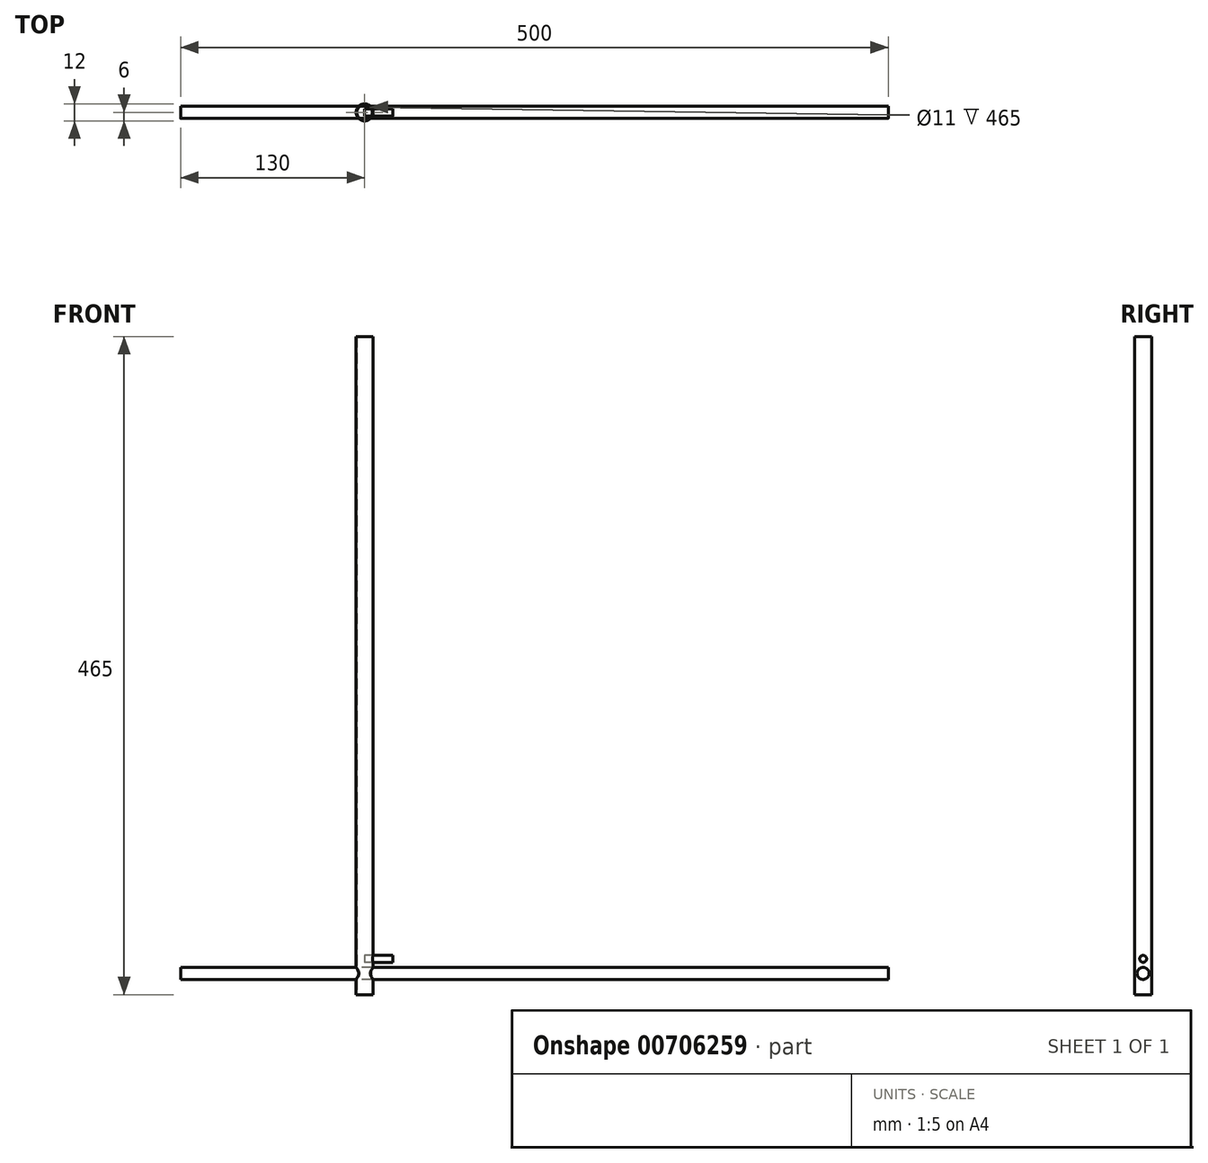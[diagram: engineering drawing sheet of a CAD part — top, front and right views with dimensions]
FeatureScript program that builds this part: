
annotation { "Feature Type Name" : "Feature", "Feature Type Description" : "" }
export const myFeature = defineFeature(function(context is Context, id is Id, definition is map)
    precondition{}
    {
        {
            var Q0;
            Q0=qCreatedBy(makeId("Top.planeOp"),FACE);
            var sketch = newSketch(context, id + "F0", { "sketchPlane" : qUnion([Q0])});
            skCircle(sketch, "E0", {"center": v(0, 0) * mm, "radius": 6 * mm});
            skCircle(sketch, "E1", {"center": v(0, 0) * mm, "radius": 5.5 * mm});
            skSolve(sketch);
        }
        {
            var Q0;
            Q0 = qSketchRegion(id + "F0", true);
            extrude(context, id + "F1", {"entities" : qUnion([Q0]), "depth" : 465 * mm, "offsetDistance" : 25 * mm});
        }
        {
            var Q0;
            Q0=qCreatedBy(makeId("Right.planeOp"),FACE);
            var sketch = newSketch(context, id + "F2", { "sketchPlane" : qUnion([Q0])});
            skCircle(sketch, "E2", {"center": v(0, 25.3) * mm, "radius": 2.44 * mm});
            skSolve(sketch);
        }
        {
            var Q0;
            Q0 = qSketchRegion(id + "F2", true);
            extrude(context, id + "F3", {"entities" : qUnion([Q0]), "operationType" : NewBodyOperationType.ADD, "depth" : 20 * mm, "offsetDistance" : 25 * mm});
        }
        {
            var Q0;
            Q0=qCreatedBy(makeId("Right.planeOp"),FACE);
            var sketch = newSketch(context, id + "F4", { "sketchPlane" : qUnion([Q0])});
            skLineSegment(sketch, "E3", {"start": v(0, 0) * mm, "end": v(0, 15) * mm});
            skCircle(sketch, "E4", {"center": v(0, 15) * mm, "radius": 4.25 * mm});
            skSolve(sketch);
        }
        {
            var Q0;
            Q0=sQuery(id+"F4.wireOp",VERTEX,"E4.center");
            var Q1;
            Q1=makeQuery(id+"F1.opExtrude","SWEPT_BODY",BODY,{"disambiguationData":[OSD([sQuery(id+"F0.wireOp",EDGE,"E0"),sQuery(id+"F0.wireOp",EDGE,"E1")])]});
            hole(context, id + "F5", {"style" : HoleStyle.SIMPLE, "endStyle" : HoleEndStyle.THROUGH, "holeDiameter" : 8 * mm, "majorDiameter" : 5 * mm, "isTappedThrough" : true, "tappedDepth" : 12 * mm, "tapClearance" : 3, "locations" : qUnion([Q0]), "scope" : qUnion([Q1])});
        }
        {
            var Q0;
            Q0=sQuery(id+"F4.wireOp",VERTEX,"E4.center");
            var Q1;
            Q1=makeQuery(id+"F1.opExtrude","SWEPT_BODY",BODY,{"disambiguationData":[OSD([sQuery(id+"F0.wireOp",EDGE,"E0"),sQuery(id+"F0.wireOp",EDGE,"E1")])]});
            hole(context, id + "F6", {"style" : HoleStyle.SIMPLE, "endStyle" : HoleEndStyle.THROUGH, "oppositeDirection" : true, "holeDiameter" : 8 * mm, "majorDiameter" : 5 * mm, "isTappedThrough" : true, "tappedDepth" : 12 * mm, "tapClearance" : 3, "locations" : qUnion([Q0]), "scope" : qUnion([Q1])});
        }
        {
            var Q0;
            Q0 = qSketchRegion(id + "F4", true);
            extrude(context, id + "F7", {"entities" : qUnion([Q0]), "operationType" : NewBodyOperationType.ADD, "endBound" : BoundingType.SYMMETRIC, "depth" : 260 * mm, "offsetDistance" : 25 * mm});
        }
        {
            var Q0;
            Q0=makeQuery(id+"F7.opExtrude","CAP_FACE",FACE,{"disambiguationData":[OSD([sQuery(id+"F4.wireOp",EDGE,"E4")])],"isStart":false});
            extrude(context, id + "F8", {"entities" : qUnion([Q0]), "operationType" : NewBodyOperationType.ADD, "depth" : 240 * mm, "offsetDistance" : 25 * mm});
        }
    });
